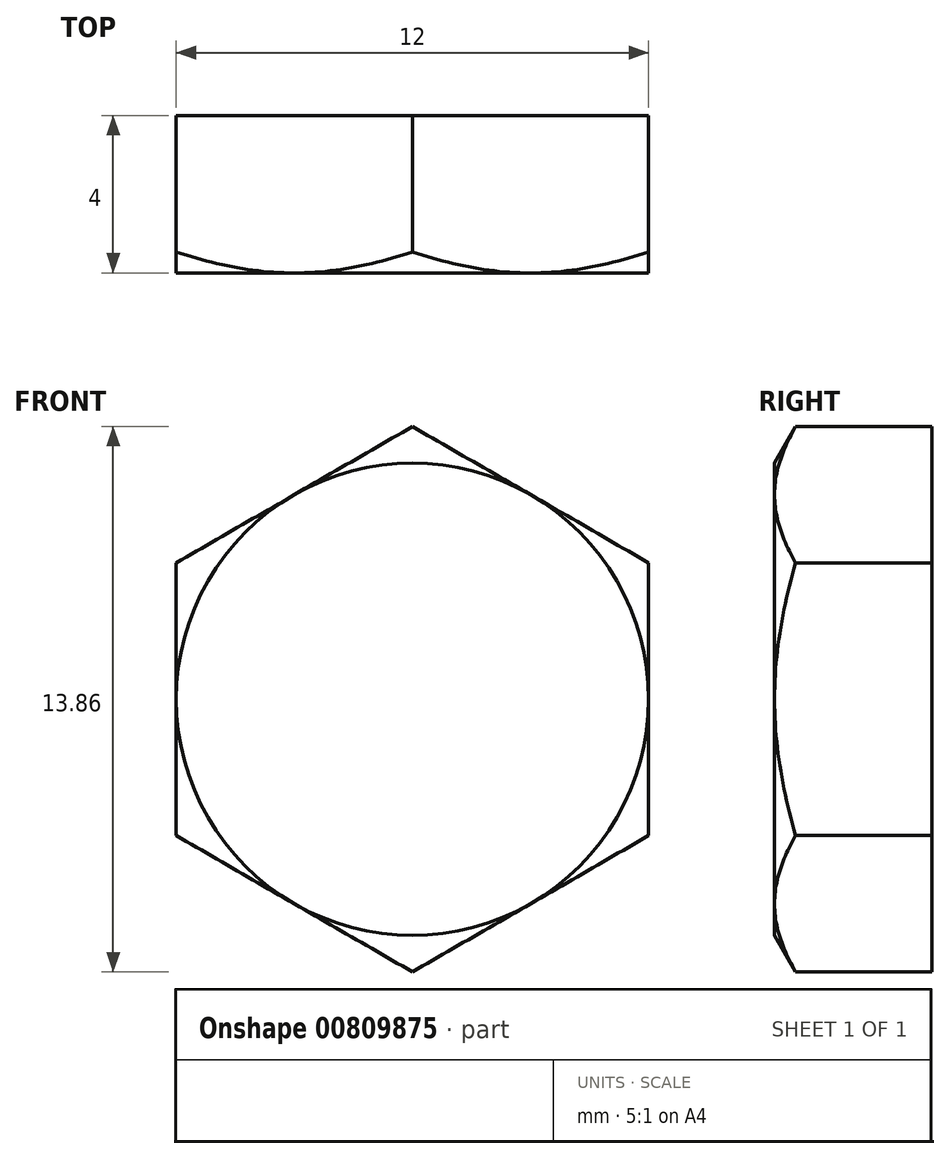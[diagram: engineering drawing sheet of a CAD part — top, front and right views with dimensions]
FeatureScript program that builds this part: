
annotation { "Feature Type Name" : "Feature", "Feature Type Description" : "" }
export const myFeature = defineFeature(function(context is Context, id is Id, definition is map)
    precondition{}
    {
        {
            var Q0;
            Q0=qCreatedBy(makeId("Front.planeOp"),FACE);
            var sketch = newSketch(context, id + "F0", { "sketchPlane" : qUnion([Q0])});
            skCircle(sketch, "E0.cCircle", {"center": v(0, 0) * mm, "radius": 6 * mm, "construction": true});
            skLineSegment(sketch, "E0.0", {"start": v(-6, 3.46) * mm, "end": v(0, 6.93) * mm});
            skLineSegment(sketch, "E0.1", {"start": v(0, 6.93) * mm, "end": v(6, 3.46) * mm});
            skLineSegment(sketch, "E0.2", {"start": v(6, 3.46) * mm, "end": v(6, -3.46) * mm});
            skLineSegment(sketch, "E0.3", {"start": v(6, -3.46) * mm, "end": v(0, -6.93) * mm});
            skLineSegment(sketch, "E0.4", {"start": v(0, -6.93) * mm, "end": v(-6, -3.46) * mm});
            skLineSegment(sketch, "E0.5", {"start": v(-6, -3.46) * mm, "end": v(-6, 3.46) * mm});
            skPoint(sketch, "E0.0.midPoint", {"position": v(-3, 5.2) * mm});
            skSolve(sketch);
        }
        {
            var Q0;
            Q0 = qSketchRegion(id + "F0", true);
            extrude(context, id + "F1", {"entities" : qUnion([Q0]), "depth" : 4 * mm, "offsetDistance" : 25 * mm});
        }
        {
            var Q0;
            Q0=qCreatedBy(makeId("Top.planeOp"),FACE);
            var sketch = newSketch(context, id + "F2", { "sketchPlane" : qUnion([Q0])});
            skLineSegment(sketch, "E1", {"start": v(6, -4) * mm, "end": v(15.13, -4) * mm});
            skLineSegment(sketch, "E2", {"start": v(15.13, -4) * mm, "end": v(15.13, 1.27) * mm});
            skLineSegment(sketch, "E3", {"start": v(15.13, 1.27) * mm, "end": v(6, -4) * mm});
            skLineSegment(sketch, "E4", {"start": v(0, -15.2) * mm, "end": v(0, 12.01) * mm, "construction": true});
            skSolve(sketch);
        }
        {
            var Q0;
            Q0=makeQuery(id+"F2.imprint","IMPRINT",FACE,{"disambiguationData":[TD([[makeQuery(id+"F2.imprint","IMPRINT",EDGE,{"derivedFrom":sQuery(id+"F2.wireOp",EDGE,"E1")}),1.0]])]});
            var Q1;
            Q1=sQuery(id+"F2.wireOp",EDGE,"E4");
            revolve(context, id + "F3", {"operationType" : NewBodyOperationType.REMOVE, "surfaceOperationType" : NewSurfaceOperationType.NEW, "entities" : qUnion([Q0]), "axis" : qUnion([Q1]), "revolveType" : RevolveType.FULL, "oppositeDirection" : true});
        }
    });
